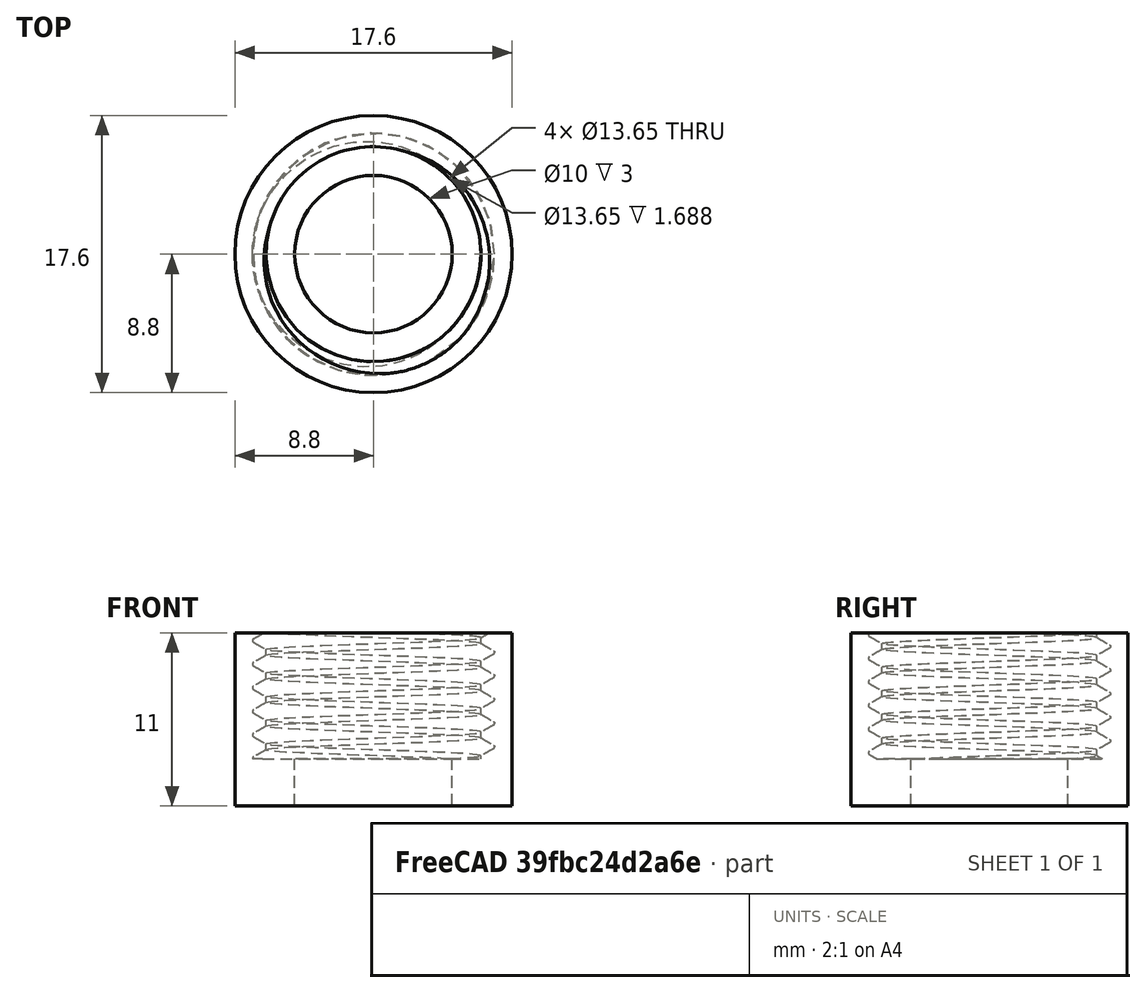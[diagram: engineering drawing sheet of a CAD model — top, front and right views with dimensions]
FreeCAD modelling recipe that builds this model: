
FCSTD DOCUMENT  (FreeCAD 0.18R16110 (Git))
Label: Gear_Rack_Nut
License: All rights reserved
LicenseURL: http://en.wikipedia.org/wiki/All_rights_reserved
objects: Part::Cylinder×4, Part::Cut×3, Spreadsheet::Sheet×2, Sketcher::SketchObject×1, Part::Helix×1, Part::Sweep×1, Part::MultiFuse×1, Mesh::Feature×1
note: 11 computed .brp shape members not serialized (recipe doc carries the construction recipe); baked Part::Feature solids carry a one-line shape summary decoded from their .brp

FEATURE [Sketcher::SketchObject] CopySketch018  label="Sketch_nut001"
  Placement = pos=(0,0,0) rot=(1,0,0;1.5708rad)
  expr: Constraints[5] = Spreadsheet006.pitch / 2
  expr: Constraints[20] = Spreadsheet006.threaddepth_tol / 12
  expr: Constraints[17] = Spreadsheet006.threaddepth_tol * (1 - 1 / 4 - 1 / 8)
  expr: Constraints[16] = Spreadsheet006.threaddepth_tol * (1 - 1 / 4) * sin(30) / cos(30)
  expr: Constraints[1] = Spreadsheet006.nut_ri - 0.001
  sketch-geometry (7):
    g0: LineSegment [constr] StartX=0 StartY=0 StartZ=0 EndX=6.82376 EndY=0 EndZ=0
    g1: LineSegment [constr] StartX=6.82376 StartY=0 StartZ=0 EndX=6.82376 EndY=-0.75 EndZ=0
    g2: LineSegment StartX=6.82376 StartY=-0.75 StartZ=0 EndX=6.82376 EndY=-0.1875 EndZ=0
    g3: LineSegment StartX=6.82376 StartY=-0.75 StartZ=0 EndX=6.82376 EndY=-1.3125 EndZ=0
    g4: LineSegment StartX=6.82376 StartY=-1.3125 StartZ=0 EndX=7.63566 EndY=-0.84375 EndZ=0
    g5: LineSegment StartX=6.82376 StartY=-0.1875 StartZ=0 EndX=7.63566 EndY=-0.65625 EndZ=0
    g6: ArcOfCircle CenterX=7.58153 CenterY=-0.75 CenterZ=0 NormalX=0 NormalY=0 NormalZ=1 AngleXU=0 Radius=0.108253 StartAngle=5.23599 EndAngle=7.33038
  constraints (21):
    c: Horizontal(g0)
    c: DistanceX(g0,g0) = 6.82376
    c: Coincident(g-1,g0)
    c: Coincident(g1,g0)
    c: Vertical(g1)
    c: DistanceY(g1,g1) = 0.75
    c: Vertical(g2)
    c: Coincident(g3,g2)
    c: Vertical(g3)
    c: Equal(g2,g3)
    c: Coincident(g4,g3)
    c: Coincident(g5,g2)
    c: Coincident(g2,g1)
    c: Equal(g5,g4)
    c: Angle(g2,g5) = 1.0472
    c: Angle(g4,g3) = 1.0472
    c: DistanceY(g3,g3) = 0.5625
    c: DistanceX(g5,g5) = 0.811899
    c: Coincident(g6,g5)
    c: Coincident(g6,g4)
    c: Radius(g6) = 0.108253
FEATURE [Spreadsheet::Sheet] Spreadsheet
  cells = A1=steigung; B1=h; D1(pitch)=1; F1=bauhöhe; G1(height)=11; A2=Gewindetiefe; B2=t; C2=h*cos(30°); D2(threaddepth)==pitch * cos(30); F2=helix height; G2(height_h)=19; C3=threaddepth tol; D3(threaddepth_tol)==(pitch + tolerance_fla * cos(30)) * cos(30); F3=Flanken - Tolerance; G3(tolerance_fla)=0; A4=Nut; F4=Radien - Tolerance; G4(tolerance)=0.2; A5=ra; E5(nut_ra)==(bolt_ri + bolt_si + threaddepth + nut_sa) * 0 + 7.7; A6=sa; E6(nut_sa)=1; A7=ri; E7(nut_ri)==(nb_centerline - threaddepth / 2 + threaddepth / 4 + tolerance) * 1 + 8 * 0; A9=Bolt; A10=ri; E10(bolt_ri)==(spring_sh + spring_sj * 0 + spring_rh) * 0 + 8 - bolt_si - threaddepth / 4 - tolerance; A11=si; E11(bolt_si)=2; G11==sqrt(1 / 6 ^ 2 - (tan(30) / 4) ^ 2) * Spreadsheet.threaddepth_tol; A12=ra; E12(bolt_ra)==nb_centerline + threaddepth / 2 - threaddepth / 8 - tolerance; A14=Nut/Bold centerline; E14(nb_centerline)==bolt_ri + bolt_si + threaddepth / 2; F14==8 - 2 - threaddepth / 8 - tolerance; A16=Spring rh; E16(spring_rh)=4.69175; A17=hülsenstärke sh; E17(spring_sh)=1; A18=join rest   js; E18(spring_sj)=1.4; A21=join heigtht jh; B21(spring_jh)=3; A22=join ri; B22(spring_jri)==spring_rh + spring_sh + tolerance_fla
FEATURE [Spreadsheet::Sheet] Spreadsheet006
  cells = A1=steigung; B1=h; D1(pitch)=1.5; F1=bauhöhe; G1(height)=8; A2=Gewindetiefe; B2=t; C2=h*cos(30°); D2(threaddepth)==pitch * cos(winkel / 2); F2=helix height; G2(height_h)=19; A3=Winkel; B3(winkel)==60°; C3=threaddepth tol; D3(threaddepth_tol)==(pitch + tolerance_fla * cos(winkel / 2)) * cos(winkel / 2); F3=Flanken - Tolerance; G3(tolerance_fla)=0; A4=Nut; F4=Radien - Tolerance; G4(tolerance)=0.2; A5=ra; E5(nut_ra)==bolt_ri + bolt_si + threaddepth + nut_sa; A6=sa; E6(nut_sa)=1.2; A7=ri; E7(nut_ri)==nb_centerline - threaddepth / 2 + threaddepth / 4 + tolerance; F7==E7 * 2; A9=Bolt; A10=ri; E10(bolt_ri)=5.1; F10==15.8 / 2; A11=si; E11(bolt_si)=1.2; G11==sqrt(1 / 6 ^ 2 - (tan(30) / 4) ^ 2) * Spreadsheet.threaddepth_tol; A12=ra; E12(bolt_ra)==nb_centerline + threaddepth / 2 - threaddepth / 8 - tolerance; F12==13.2 / 2; A14=Nut/Bold centerline; E14(nb_centerline)==bolt_ri + bolt_si + threaddepth / 2; F14==18.3 / 2; A16=Spring rh; E16(spring_rh)=1.8; A17=hülsenstärke sh; E17(spring_sh)=1; A18=join rest   js; E18(spring_sj)=1.4; A21=join heigtht jh; B21(spring_jh)=3; A22=join ri; B22(spring_jri)==spring_rh + spring_sh + tolerance_fla
FEATURE [Part::Cylinder] Cylinder185  label="Zylinder185"
  Angle = 360
  AttacherType = Attacher::AttachEngine3D
  Height = 8
  Radius = 8.79904
  expr: Radius = Spreadsheet006.E5
FEATURE [Part::Cylinder] Cylinder188  label="Zylinder188"
  Angle = 360
  AttacherType = Attacher::AttachEngine3D
  Height = 3
  Radius = 5
  expr: Height = 3
FEATURE [Part::Cylinder] Cylinder187  label="Zylinder187"
  Angle = 360
  AttacherType = Attacher::AttachEngine3D
  Height = 3
  Radius = 8.79904
  expr: Radius = Spreadsheet006.E5
FEATURE [Part::Cut] Cut016
  Base = -> Cylinder187
  Placement = pos=(0,0,-3) rot=(0,0,1;0rad)
  Tool = -> Cylinder188
FEATURE [Part::Cylinder] Cylinder186  label="Zylinder186"
  Angle = 360
  AttacherType = Attacher::AttachEngine3D
  Height = 8
  Radius = 6.82476
  expr: Radius = Spreadsheet006.E7
FEATURE [Part::Cut] Cut014
  Base = -> Cylinder185
  Tool = -> Cylinder186
FEATURE [Part::Helix] Helix
  Angle = 0
  AttacherType = Attacher::AttachEngine3D
  Height = 15
  LocalCoord = 0
  Pitch = 1.5
  Radius = 6.82476
  Style = 1
  expr: Radius = Spreadsheet006.E7
  expr: Height = 15
  expr: Pitch = Spreadsheet006.D1
FEATURE [Part::Sweep] Sweep012
  Frenet = true
  Sections = -> [CopySketch018]
  Solid = true
  Spine = -> Helix [Edge1,Edge2,Edge3,Edge4,Edge5,Edge6,Edge7]
  Transition = 1
FEATURE [Part::Cut] Cut015
  Base = -> Cut014
  Tool = -> Sweep012
FEATURE [Part::MultiFuse] Fusion001  label="Gear_Rack_Nut"
  Shapes = -> [Cut016,Cut015]
FEATURE [Mesh::Feature] Mesh  label="Gear_Rack_Nut (Meshed)"
